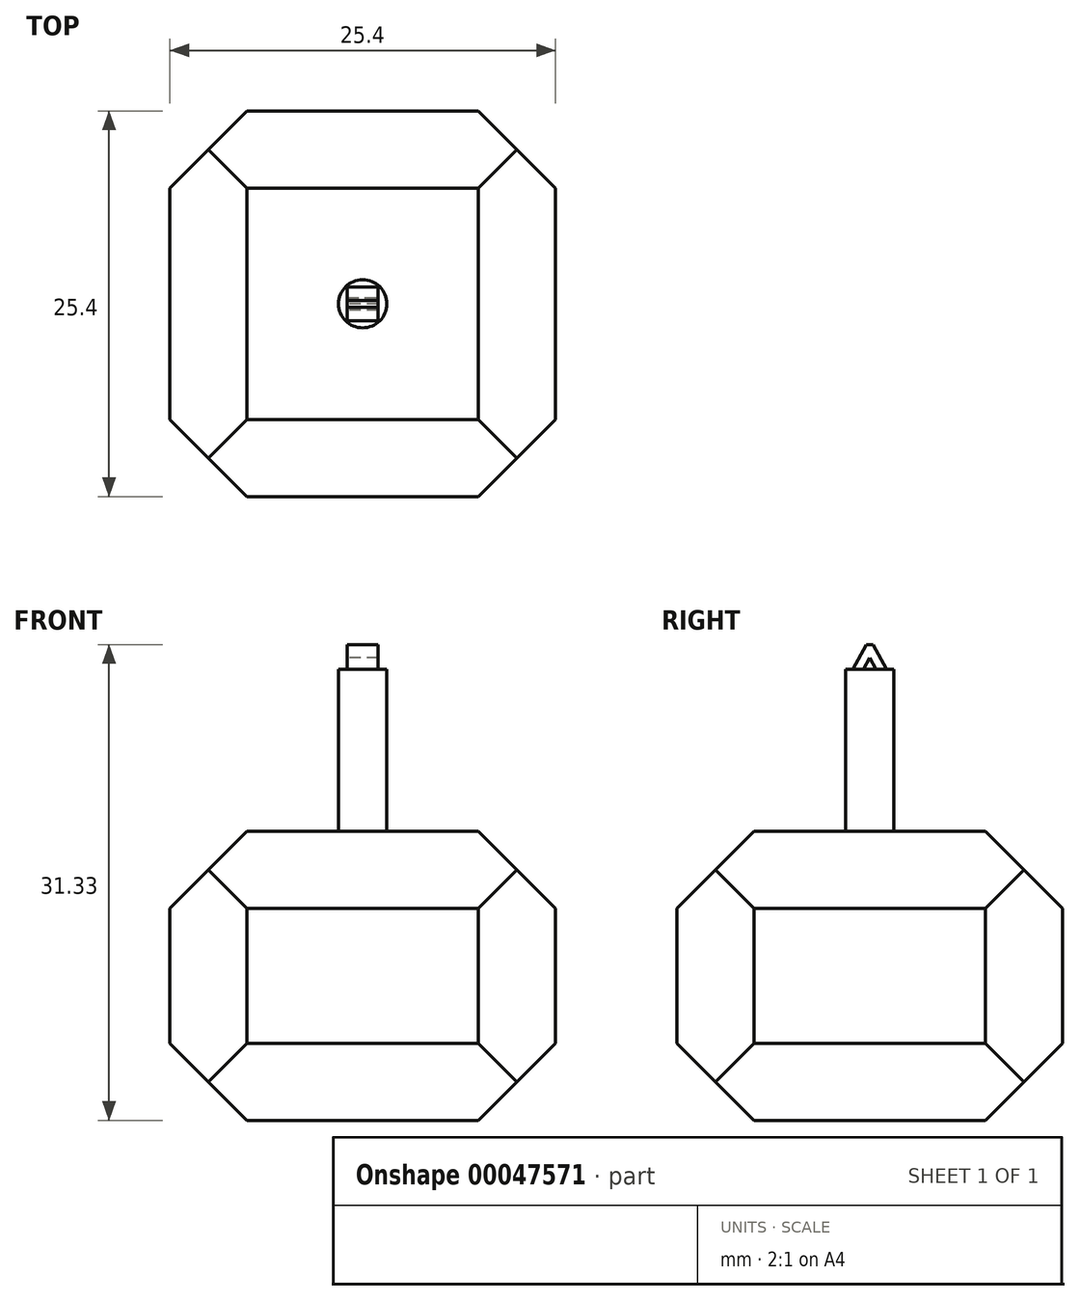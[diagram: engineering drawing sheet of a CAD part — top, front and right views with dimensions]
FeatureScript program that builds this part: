
annotation { "Feature Type Name" : "Feature", "Feature Type Description" : "" }
export const myFeature = defineFeature(function(context is Context, id is Id, definition is map)
    precondition{}
    {
        {
            var Q0;
            Q0=qCreatedBy(makeId("Front.planeOp"),FACE);
            var sketch = newSketch(context, id + "F0", { "sketchPlane" : qUnion([Q0])});
            skLineSegment(sketch, "E0.bottom", {"start": v(0, -38.58) * mm, "end": v(-12.7, -38.58) * mm});
            skLineSegment(sketch, "E0.top", {"start": v(0, -19.53) * mm, "end": v(-12.7, -19.53) * mm});
            skLineSegment(sketch, "E0.left", {"start": v(0, -38.58) * mm, "end": v(0, -19.53) * mm, "construction": true});
            skLineSegment(sketch, "E0.right", {"start": v(-12.7, -38.58) * mm, "end": v(-12.7, -19.53) * mm});
            skLineSegment(sketch, "E1.bottom", {"start": v(0, -19.53) * mm, "end": v(0, -19.53) * mm});
            skLineSegment(sketch, "E1.top", {"start": v(0, -38.58) * mm, "end": v(0, -38.58) * mm});
            skLineSegment(sketch, "E1.left", {"start": v(0, -19.53) * mm, "end": v(0, -38.58) * mm, "construction": true});
            skLineSegment(sketch, "E1.right", {"start": v(0, -19.53) * mm, "end": v(0, -38.58) * mm, "construction": true});
            skLineSegment(sketch, "E2.MirrorCS", {"start": v(0, -38.58) * mm, "end": v(12.7, -38.58) * mm, "construction": true});
            skLineSegment(sketch, "E3.MirrorCS", {"start": v(0, -19.53) * mm, "end": v(12.7, -19.53) * mm, "construction": true});
            skLineSegment(sketch, "E4.MirrorCS", {"start": v(12.7, -38.58) * mm, "end": v(12.7, -19.53) * mm, "construction": true});
            skLineSegment(sketch, "E5.MirrorCS", {"start": v(12.7, -38.58) * mm, "end": v(12.7, -19.53) * mm});
            skLineSegment(sketch, "E6.MirrorCS", {"start": v(0, -38.58) * mm, "end": v(12.7, -38.58) * mm});
            skLineSegment(sketch, "E7.MirrorCS", {"start": v(0, -19.53) * mm, "end": v(12.7, -19.53) * mm});
            skSolve(sketch);
        }
        {
            var Q0;
            Q0=makeQuery(id+"F0.imprint","IMPRINT",FACE,{"disambiguationData":[TD([[makeQuery(id+"F0.imprint","IMPRINT",EDGE,{"derivedFrom":sQuery(id+"F0.wireOp",EDGE,"E0.bottom")}),-1.0]])]});
            extrude(context, id + "F1", {"entities" : qUnion([Q0]), "endBound" : BoundingType.SYMMETRIC, "depth" : 25.4 * mm});
        }
        {
            var Q0;
            Q0=makeQuery(id+"F1.opExtrude","CAP_EDGE",EDGE,{"disambiguationData":[OSD([sQuery(id+"F0.wireOp",EDGE,"E0.top"),sQuery(id+"F0.wireOp",EDGE,"E7.MirrorCS")])],"isStart":false});
            var Q1;
            Q1=makeQuery(id+"F1.opExtrude","SWEPT_EDGE",EDGE,{"disambiguationData":[OSD([sQuery(id+"F0.wireOp",EDGE,"E5.MirrorCS"),sQuery(id+"F0.wireOp",EDGE,"E7.MirrorCS")])]});
            var Q2;
            Q2=makeQuery(id+"F1.opExtrude","SWEPT_EDGE",EDGE,{"disambiguationData":[OSD([sQuery(id+"F0.wireOp",EDGE,"E0.top"),sQuery(id+"F0.wireOp",EDGE,"E0.right")])]});
            var Q3;
            Q3=makeQuery(id+"F1.opExtrude","CAP_EDGE",EDGE,{"disambiguationData":[OSD([sQuery(id+"F0.wireOp",EDGE,"E0.top"),sQuery(id+"F0.wireOp",EDGE,"E7.MirrorCS")])],"isStart":true});
            var Q4;
            Q4=makeQuery(id+"F1.opExtrude","SWEPT_EDGE",EDGE,{"disambiguationData":[OSD([sQuery(id+"F0.wireOp",EDGE,"E0.bottom"),sQuery(id+"F0.wireOp",EDGE,"E0.right")])]});
            var Q5;
            Q5=makeQuery(id+"F1.opExtrude","CAP_EDGE",EDGE,{"disambiguationData":[OSD([sQuery(id+"F0.wireOp",EDGE,"E0.bottom"),sQuery(id+"F0.wireOp",EDGE,"E6.MirrorCS")])],"isStart":false});
            var Q6;
            Q6=makeQuery(id+"F1.opExtrude","SWEPT_EDGE",EDGE,{"disambiguationData":[OSD([sQuery(id+"F0.wireOp",EDGE,"E5.MirrorCS"),sQuery(id+"F0.wireOp",EDGE,"E6.MirrorCS")])]});
            var Q7;
            Q7=makeQuery(id+"F1.opExtrude","CAP_EDGE",EDGE,{"disambiguationData":[OSD([sQuery(id+"F0.wireOp",EDGE,"E0.bottom"),sQuery(id+"F0.wireOp",EDGE,"E6.MirrorCS")])],"isStart":true});
            chamfer(context, id + "F2", {"entities" : qUnion([Q0, Q1, Q2, Q3, Q4, Q5, Q6, Q7]), "width" : 5.08 * mm, "tangentPropagation" : true});
        }
        {
            var Q0;
            Q0=qCreatedBy(makeId("Top.planeOp"),FACE);
            cPlane(context, id + "F3", {"entities" : qUnion([Q0]), "cplaneType" : CPlaneType.OFFSET, "offset" : 8.9 * mm, "oppositeDirection" : true, "width" : 152.4 * mm, "height" : 152.4 * mm});
        }
        {
            var Q0;
            Q0=qCreatedBy(id+"F3.planeOp",FACE);
            var sketch = newSketch(context, id + "F4", { "sketchPlane" : qUnion([Q0])});
            skCircle(sketch, "E8", {"center": v(0, 0) * mm, "radius": 1.59 * mm});
            skSolve(sketch);
        }
        {
            var Q0;
            Q0=makeQuery(id+"F4.imprint","IMPRINT",FACE,{"disambiguationData":[TD([[makeQuery(id+"F4.imprint","IMPRINT",EDGE,{"derivedFrom":sQuery(id+"F4.wireOp",EDGE,"E8")}),1.0]])]});
            extrude(context, id + "F5", {"entities" : qUnion([Q0]), "operationType" : NewBodyOperationType.ADD, "oppositeDirection" : true, "depth" : 11.73 * mm});
        }
        {
            var Q0;
            Q0=makeQuery(id+"F1.opExtrude","CAP_EDGE",EDGE,{"disambiguationData":[OSD([sQuery(id+"F0.wireOp",EDGE,"E0.right")])],"isStart":true});
            var Q1;
            Q1=makeQuery(id+"F1.opExtrude","CAP_EDGE",EDGE,{"disambiguationData":[OSD([sQuery(id+"F0.wireOp",EDGE,"E5.MirrorCS")])],"isStart":true});
            var Q2;
            Q2=makeQuery(id+"F1.opExtrude","CAP_EDGE",EDGE,{"disambiguationData":[OSD([sQuery(id+"F0.wireOp",EDGE,"E5.MirrorCS")])],"isStart":false});
            var Q3;
            Q3=makeQuery(id+"F1.opExtrude","CAP_EDGE",EDGE,{"disambiguationData":[OSD([sQuery(id+"F0.wireOp",EDGE,"E0.right")])],"isStart":false});
            chamfer(context, id + "F6", {"entities" : qUnion([Q0, Q1, Q2, Q3]), "width" : 5.08 * mm, "tangentPropagation" : true});
        }
        {
            var Q0;
            Q0=qCreatedBy(makeId("Right.planeOp"),FACE);
            var sketch = newSketch(context, id + "F7", { "sketchPlane" : qUnion([Q0])});
            skLineSegment(sketch, "E9", {"start": v(1.13, -8.92) * mm, "end": v(0.43, -8.92) * mm});
            skLineSegment(sketch, "E10", {"start": v(0.43, -8.92) * mm, "end": v(0, -8.12) * mm});
            skLineSegment(sketch, "E11", {"start": v(0, -8.12) * mm, "end": v(-0.44, -8.9) * mm});
            skLineSegment(sketch, "E12", {"start": v(-0.44, -8.9) * mm, "end": v(-1.14, -8.9) * mm});
            skLineSegment(sketch, "E13", {"start": v(-1.14, -8.9) * mm, "end": v(0, -6.85) * mm});
            skLineSegment(sketch, "E14", {"start": v(0, -6.85) * mm, "end": v(1.13, -8.92) * mm});
            skSolve(sketch);
        }
        {
            var Q0;
            Q0=makeQuery(id+"F7.imprint","IMPRINT",FACE,{"disambiguationData":[TD([[makeQuery(id+"F7.imprint","IMPRINT",EDGE,{"derivedFrom":sQuery(id+"F7.wireOp",EDGE,"E9")}),-1.0]])]});
            extrude(context, id + "F8", {"entities" : qUnion([Q0]), "operationType" : NewBodyOperationType.ADD, "endBound" : BoundingType.SYMMETRIC, "depth" : 2.04 * mm});
        }
        {
            var Q0;
            Q0=makeQuery(id+"F8.opExtrude","SWEPT_EDGE",EDGE,{"disambiguationData":[OSD([sQuery(id+"F7.wireOp",EDGE,"E13"),sQuery(id+"F7.wireOp",EDGE,"E14")])]});
            chamfer(context, id + "F9", {"entities" : qUnion([Q0]), "width" : 0.25 * mm, "tangentPropagation" : true});
        }
    });
